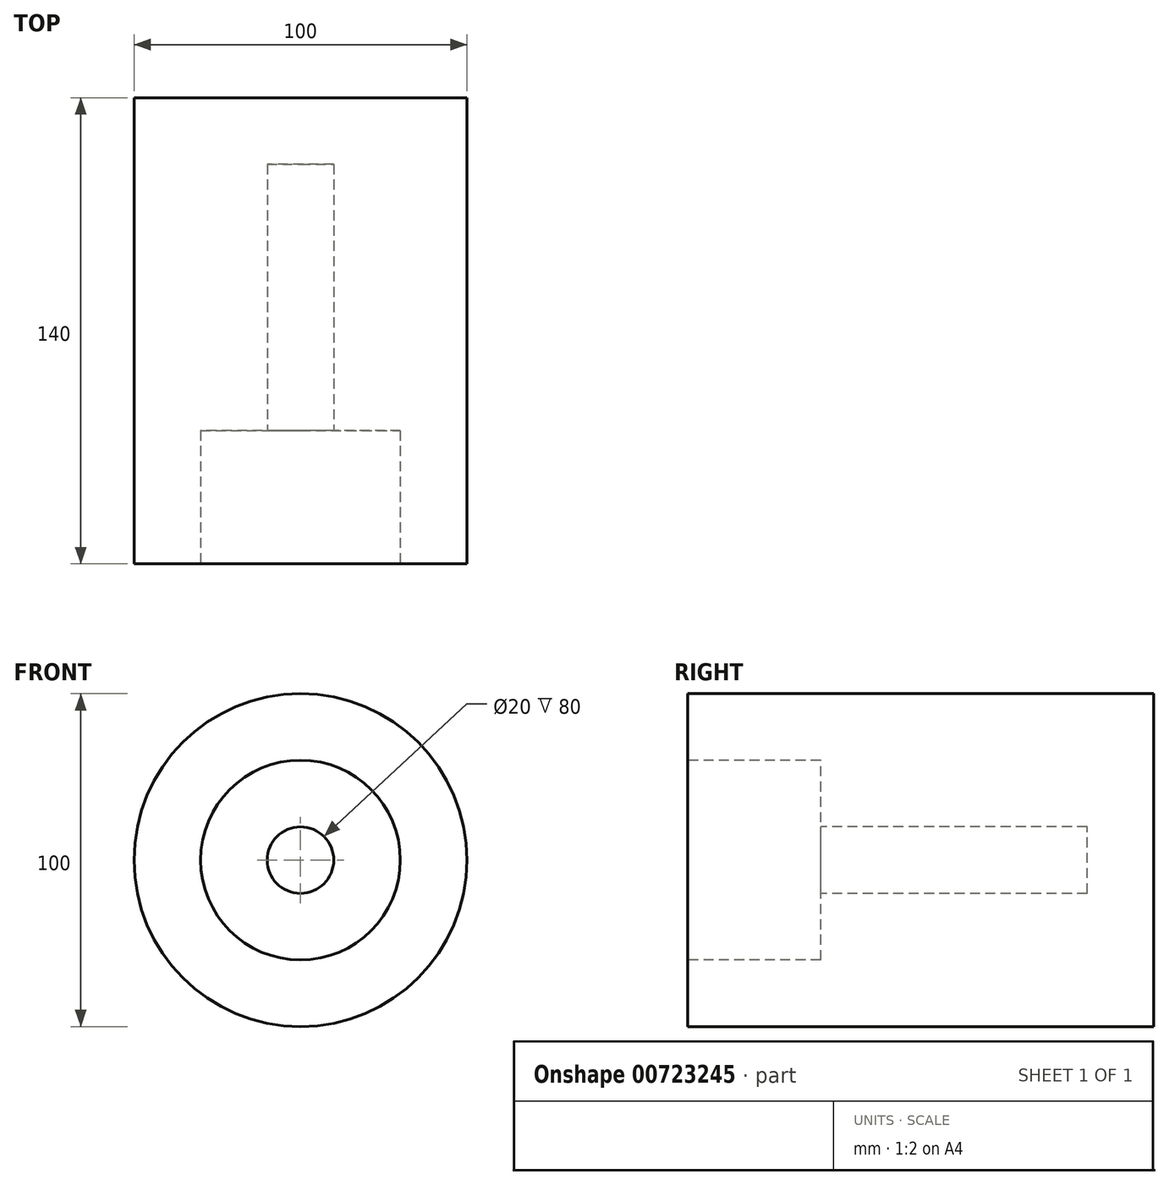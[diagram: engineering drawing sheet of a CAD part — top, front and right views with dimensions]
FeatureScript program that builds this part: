
annotation { "Feature Type Name" : "Feature", "Feature Type Description" : "" }
export const myFeature = defineFeature(function(context is Context, id is Id, definition is map)
    precondition{}
    {
        {
            var Q0;
            Q0=qCreatedBy(makeId("Front.planeOp"),FACE);
            var sketch = newSketch(context, id + "F0", { "sketchPlane" : qUnion([Q0])});
            skCircle(sketch, "E0", {"center": v(0, 0) * mm, "radius": 50 * mm});
            skSolve(sketch);
        }
        {
            var Q0;
            Q0 = qSketchRegion(id + "F0", true);
            extrude(context, id + "F1", {"entities" : qUnion([Q0]), "depth" : 140 * mm, "offsetDistance" : 25.4 * mm});
        }
        {
            var Q0;
            Q0=makeQuery(id+"F1.opExtrude","CAP_FACE",FACE,{"disambiguationData":[OSD([sQuery(id+"F0.wireOp",EDGE,"E0")])],"isStart":false});
            var sketch = newSketch(context, id + "F2", { "sketchPlane" : qUnion([Q0])});
            skCircle(sketch, "E1", {"center": v(0, 0) * mm, "radius": 30 * mm});
            skSolve(sketch);
        }
        {
            var Q0;
            Q0 = qSketchRegion(id + "F2", true);
            extrude(context, id + "F3", {"entities" : qUnion([Q0]), "operationType" : NewBodyOperationType.REMOVE, "oppositeDirection" : true, "depth" : 40 * mm, "offsetDistance" : 25.4 * mm});
        }
        {
            var Q0;
            Q0=makeQuery(id+"F3.boolean.opBoolean","COPY",FACE,{"derivedFrom":makeQuery(id+"F3.opExtrude","CAP_FACE",FACE,{"disambiguationData":[OSD([sQuery(id+"F2.wireOp",EDGE,"E1")])],"isStart":false})});
            var sketch = newSketch(context, id + "F4", { "sketchPlane" : qUnion([Q0])});
            skCircle(sketch, "E2", {"center": v(0, 0) * mm, "radius": 10 * mm});
            skSolve(sketch);
        }
        {
            var Q0;
            Q0 = qSketchRegion(id + "F4", true);
            extrude(context, id + "F5", {"entities" : qUnion([Q0]), "operationType" : NewBodyOperationType.REMOVE, "oppositeDirection" : true, "depth" : 80 * mm, "offsetDistance" : 25.4 * mm});
        }
    });
